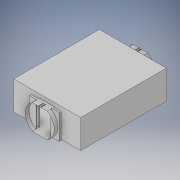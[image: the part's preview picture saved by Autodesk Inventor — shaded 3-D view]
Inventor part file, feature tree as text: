
AUTODESK INVENTOR PART (.ipt)
format: ipt  version: 2017 (Build 210142000, 142)  size: 273,408 bytes
history: native  units: in
note: dims shown in document units (in); Inventor stores cm internally (conversion verified against a paired STEP export)
features: extrude x7, sketch x7, mirror x3, other x1, delete_face x1
ambient origin geometry x8: Origin, YZ Plane, XZ Plane, XY Plane, X Axis, Y Axis, Z Axis, Center Point
bodies: Solid1 (feature_tree)
feature tree (19):
  extrude  "floor"  Depth=25.0in
  extrude  "walls"  Depth=1.0in
  extrude  "doorframe"  Depth=1.0in
  extrude  "ceiling"  Depth=1.0in TaperAngle=0.0deg
  extrude  "left door slot"  Depth=6.6667in
  mirror  "mirror door slot"
  mirror  "right door slot"
  sketch  "Sketch10"  dims[d20=8.6667in d21=0.0in d22=1.0in d23=0.0in]
  extrude  "corridor connect"  Depth=1.0in TaperAngle=0.0deg
  other  "middle of the room"
  extrude  "reveil rest of light"  Depth=0.5in
  mirror  "Mirror connection for starting door"
  delete_face  "Delete Face1"
  sketch  "Sketch1"  dims[d0=20.0in d1=25.0in]
  sketch  "Sketch4"  dims[d2=1.0in d3=0.0in d11=1.0in]
  sketch  "Sketch5"  dims[d12=1.0in d13=1.0in]
  sketch  "Sketch7"  dims[d14=1.0in d15=8.6667in d16=0.0in]
  sketch  "Sketch8"  dims[d17=2.0in d18=6.6667in]
  sketch  "Sketch13"  dims[d24=0.25in d25=0.5in d26=2.0in d27=0.0in d28=6.6667in d37=6.6667in d40=1.0in d41=0.0in d58=4.0in d59=0.5833in d60=3.8873in d61=3.8873in d62=1.7083in d63=0.0625in d64=0.0625in d65=1.6458in d66=0.25in d67=0.125in d69=0.0884in d70=45.0deg d71=3.3333in d72=0.125in d73=1.0in d74=1.0in d75=0.0in]
